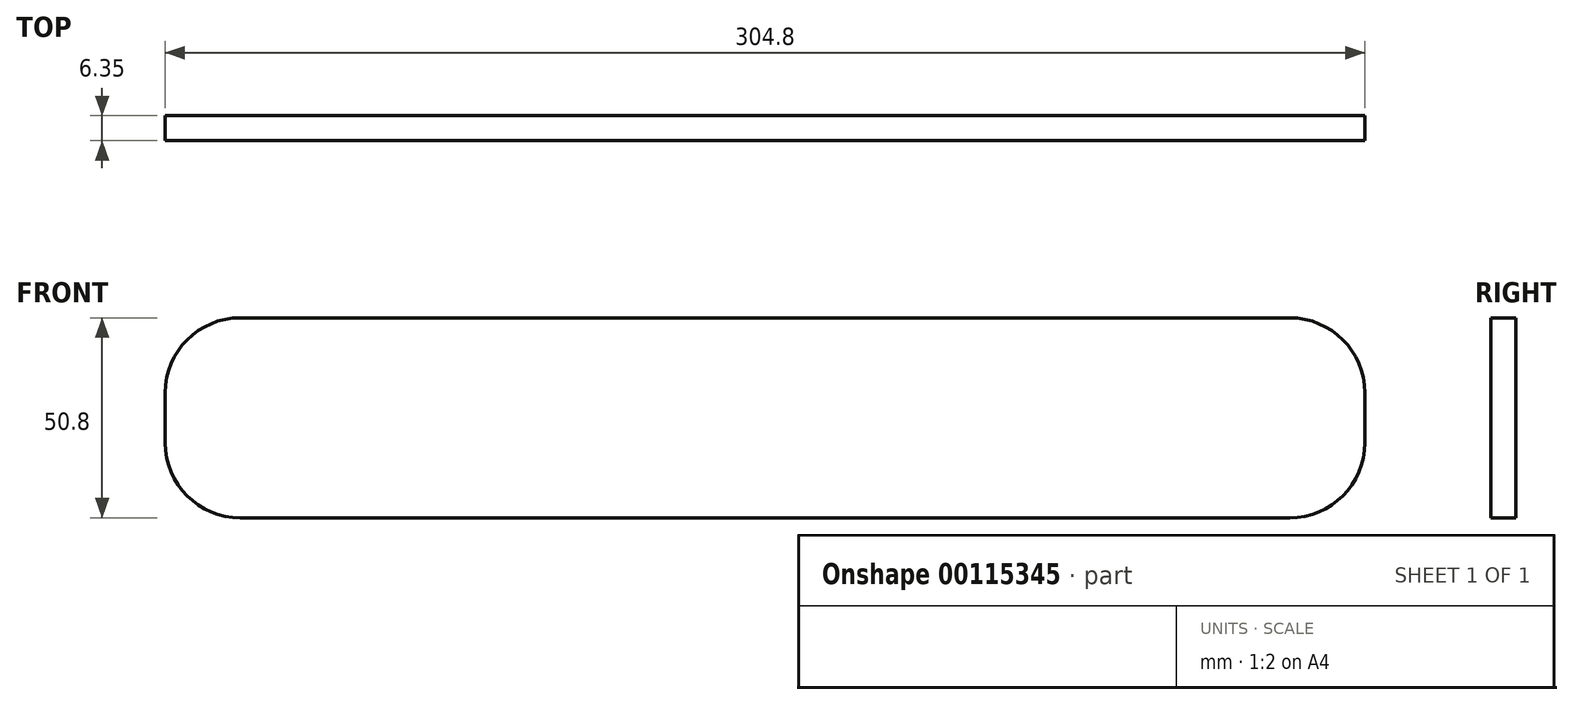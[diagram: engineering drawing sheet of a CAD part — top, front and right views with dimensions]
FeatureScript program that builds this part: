
annotation { "Feature Type Name" : "Feature", "Feature Type Description" : "" }
export const myFeature = defineFeature(function(context is Context, id is Id, definition is map)
    precondition{}
    {
        {
            var Q0;
            Q0=qCreatedBy(makeId("Front.planeOp"),FACE);
            var sketch = newSketch(context, id + "F0", { "sketchPlane" : qUnion([Q0])});
            skLineSegment(sketch, "E0.bottom", {"start": v(-147.78, 13.66) * mm, "end": v(157.02, 13.66) * mm});
            skLineSegment(sketch, "E0.top", {"start": v(-147.78, -37.14) * mm, "end": v(157.02, -37.14) * mm});
            skLineSegment(sketch, "E0.left", {"start": v(-147.78, 13.66) * mm, "end": v(-147.78, -37.14) * mm});
            skLineSegment(sketch, "E0.right", {"start": v(157.02, 13.66) * mm, "end": v(157.02, -37.14) * mm});
            skSolve(sketch);
        }
        {
            var Q0;
            Q0=makeQuery(id+"F0.imprint","IMPRINT",FACE,{"disambiguationData":[TD([[makeQuery(id+"F0.imprint","IMPRINT",EDGE,{"derivedFrom":sQuery(id+"F0.wireOp",EDGE,"E0.bottom")}),-1.0]])]});
            extrude(context, id + "F1", {"entities" : qUnion([Q0]), "depth" : 6.35 * mm});
        }
        {
            var Q0;
            Q0=makeQuery(id+"F1.opExtrude","SWEPT_EDGE",EDGE,{"disambiguationData":[OSD([sQuery(id+"F0.wireOp",EDGE,"E0.bottom"),sQuery(id+"F0.wireOp",EDGE,"E0.left")])]});
            var Q1;
            Q1=makeQuery(id+"F1.opExtrude","SWEPT_EDGE",EDGE,{"disambiguationData":[OSD([sQuery(id+"F0.wireOp",EDGE,"E0.top"),sQuery(id+"F0.wireOp",EDGE,"E0.left")])]});
            var Q2;
            Q2=makeQuery(id+"F1.opExtrude","SWEPT_EDGE",EDGE,{"disambiguationData":[OSD([sQuery(id+"F0.wireOp",EDGE,"E0.bottom"),sQuery(id+"F0.wireOp",EDGE,"E0.right")])]});
            var Q3;
            Q3=makeQuery(id+"F1.opExtrude","SWEPT_EDGE",EDGE,{"disambiguationData":[OSD([sQuery(id+"F0.wireOp",EDGE,"E0.top"),sQuery(id+"F0.wireOp",EDGE,"E0.right")])]});
            fillet(context, id + "F2", {"entities" : qUnion([Q0, Q1, Q2, Q3]), "radius" : 19.05 * mm, "tangentPropagation" : true, "allowEdgeOverflow" : false});
        }
    });
